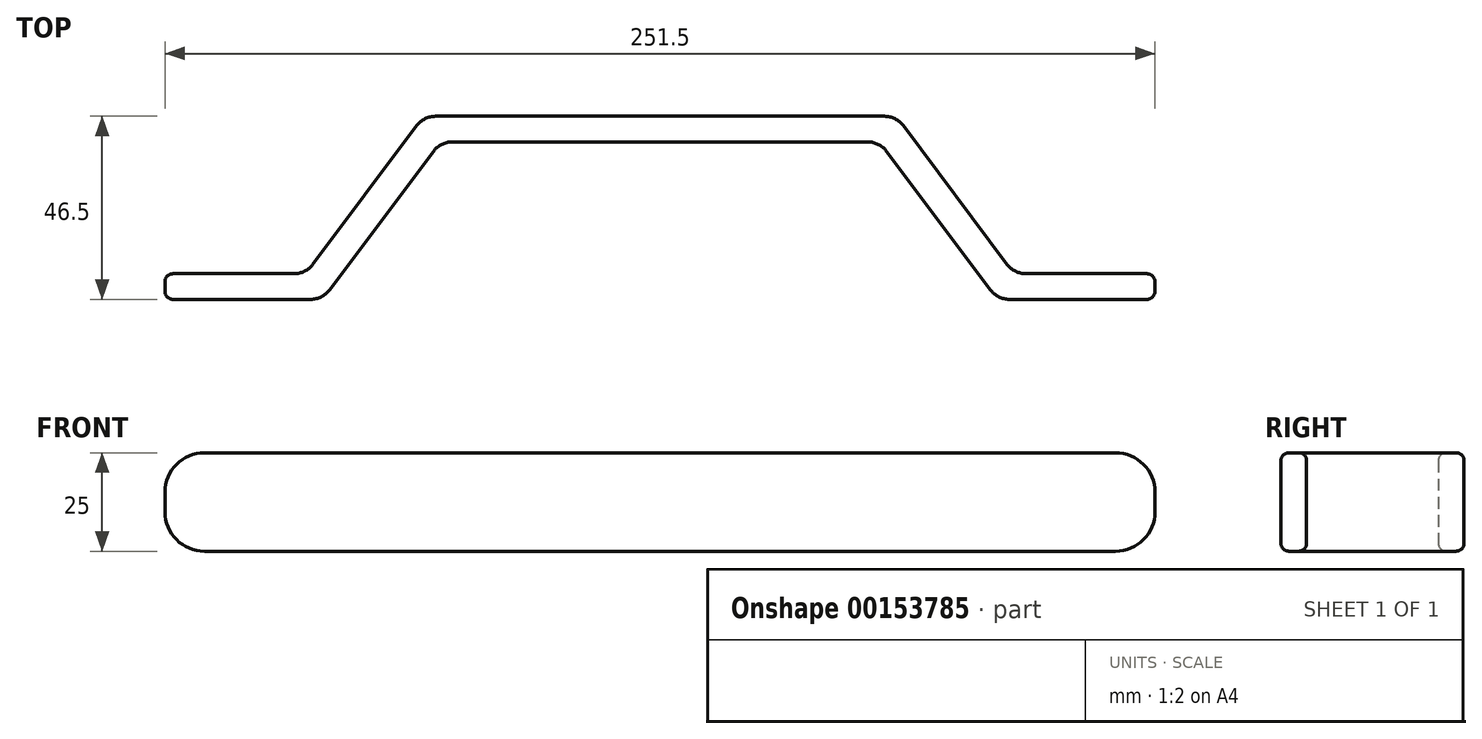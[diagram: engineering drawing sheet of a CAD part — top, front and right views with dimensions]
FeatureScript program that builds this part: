
annotation { "Feature Type Name" : "Feature", "Feature Type Description" : "" }
export const myFeature = defineFeature(function(context is Context, id is Id, definition is map)
    precondition{}
    {
        {
            var Q0;
            Q0=qCreatedBy(makeId("Top.planeOp"),FACE);
            var sketch = newSketch(context, id + "F0", { "sketchPlane" : qUnion([Q0])});
            skLineSegment(sketch, "E0", {"start": v(0, 0) * mm, "end": v(37, 0) * mm});
            skLineSegment(sketch, "E1", {"start": v(41.8, 2.4) * mm, "end": v(68.2, 37.6) * mm});
            skLineSegment(sketch, "E2", {"start": v(73, 40) * mm, "end": v(130, 40) * mm});
            skPoint(sketch, "E3.visualSharp", {"position": v(70, 40) * mm});
            skArc(sketch, "E3.filletArc", {"start": v(73, 40) * mm, "mid": v(70.32, 39.37) * mm, "end": v(68.2, 37.6) * mm});
            skPoint(sketch, "E4.visualSharp", {"position": v(40, 0) * mm});
            skArc(sketch, "E4.filletArc", {"start": v(37, 0) * mm, "mid": v(39.68, 0.63) * mm, "end": v(41.8, 2.4) * mm});
            skPoint(sketch, "E5.0.1.0", {"position": v(35.75, 6.5) * mm});
            skPoint(sketch, "E5.0.1.1", {"position": v(65.75, 46.5) * mm});
            skLineSegment(sketch, "E5.0.1.2", {"start": v(68.75, 46.5) * mm, "end": v(125.75, 46.5) * mm});
            skLineSegment(sketch, "E5.0.1.3", {"start": v(37.55, 8.9) * mm, "end": v(63.95, 44.1) * mm});
            skLineSegment(sketch, "E5.0.1.4", {"start": v(-4.25, 6.5) * mm, "end": v(32.75, 6.5) * mm});
            skArc(sketch, "E5.0.1.5", {"start": v(32.75, 6.5) * mm, "mid": v(35.43, 7.13) * mm, "end": v(37.55, 8.9) * mm});
            skArc(sketch, "E5.0.1.6", {"start": v(68.75, 46.5) * mm, "mid": v(66.07, 45.87) * mm, "end": v(63.95, 44.1) * mm});
            skLineSegment(sketch, "E5.direction1", {"start": v(0, 0) * mm, "end": v(25, 0) * mm, "construction": true});
            skLineSegment(sketch, "E5.direction2", {"start": v(0, 0) * mm, "end": v(-4.25, 6.5) * mm, "construction": true});
            skLineSegment(sketch, "E6", {"start": v(0, 0) * mm, "end": v(0, 6.5) * mm});
            skLineSegment(sketch, "E7", {"start": v(125.75, 46.5) * mm, "end": v(125.75, 40) * mm});
            skSolve(sketch);
        }
        {
            var Q0;
            Q0 = qSketchRegion(id + "F0", true);
            extrude(context, id + "F1", {"entities" : qUnion([Q0]), "depth" : 25 * mm});
        }
        {
            var Q0;
            Q0=makeQuery(id+"F1.opExtrude","CAP_EDGE",EDGE,{"disambiguationData":[OSD([sQuery(id+"F0.wireOp",EDGE,"E6")])],"isStart":false});
            var Q1;
            Q1=makeQuery(id+"F1.opExtrude","CAP_EDGE",EDGE,{"disambiguationData":[OSD([sQuery(id+"F0.wireOp",EDGE,"E6")])],"isStart":true});
            fillet(context, id + "F2", {"entities" : qUnion([Q0, Q1]), "radius" : 10 * mm, "tangentPropagation" : true, "allowEdgeOverflow" : false});
        }
        {
            var Q0;
            Q0=makeQuery(id+"F1.opExtrude","CAP_EDGE",EDGE,{"disambiguationData":[OSD([sQuery(id+"F0.wireOp",EDGE,"E2")])],"isStart":false});
            var Q1;
            Q1=makeQuery(id+"F1.opExtrude","CAP_EDGE",EDGE,{"disambiguationData":[OSD([sQuery(id+"F0.wireOp",EDGE,"E5.0.1.2")])],"isStart":false});
            fillet(context, id + "F3", {"entities" : qUnion([Q0, Q1]), "radius" : 2 * mm, "tangentPropagation" : true, "allowEdgeOverflow" : false});
        }
        {
            var Q0;
            Q0=makeQuery(id+"F1.opExtrude","SWEPT_BODY",BODY,{"disambiguationData":[OSD([sQuery(id+"F0.wireOp",EDGE,"E0"),sQuery(id+"F0.wireOp",EDGE,"E1"),sQuery(id+"F0.wireOp",EDGE,"E2"),sQuery(id+"F0.wireOp",EDGE,"E3.filletArc"),sQuery(id+"F0.wireOp",EDGE,"E4.filletArc"),sQuery(id+"F0.wireOp",EDGE,"E5.0.1.2"),sQuery(id+"F0.wireOp",EDGE,"E5.0.1.3"),sQuery(id+"F0.wireOp",EDGE,"E5.0.1.4"),sQuery(id+"F0.wireOp",EDGE,"E5.0.1.5"),sQuery(id+"F0.wireOp",EDGE,"E5.0.1.6"),sQuery(id+"F0.wireOp",EDGE,"E6"),sQuery(id+"F0.wireOp",EDGE,"E7")])]});
            var Q1;
            Q1=makeQuery(id+"F1.opExtrude","SWEPT_FACE",FACE,{"disambiguationData":[OSD([sQuery(id+"F0.wireOp",EDGE,"E7")])]});
            mirror(context, id + "F4", {"operationType" : NewBodyOperationType.ADD, "entities" : qUnion([Q0]), "mirrorPlane" : qUnion([Q1])});
        }
    });
